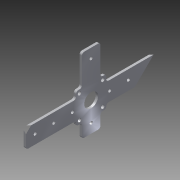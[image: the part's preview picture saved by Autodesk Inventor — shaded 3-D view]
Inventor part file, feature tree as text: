
AUTODESK INVENTOR PART (.ipt)
format: ipt  version: 2014 SP1 (Build 180222100, 222)  size: 162,816 bytes
history: native  units: in
note: dims shown in document units (in); Inventor stores cm internally (conversion verified against a paired STEP export)
features: extrude x2, sketch x2
ambient origin geometry x8: Origin, YZ Plane, XZ Plane, XY Plane, X Axis, Y Axis, Z Axis, Center Point
bodies: Solid1 (feature_tree)
feature tree (4):
  extrude  "Extrusion1"  Depth=4.0in
  extrude  "Extrusion2"  Depth=1.625in
  sketch  "Sketch1"  dims[d0=1.0in d1=4.0in]
  sketch  "Sketch2"  dims[d2=1.625in d3=1.625in d5=0.164in d6=0.164in d7=1.25in d8=1.25in d10=0.1875in d11=0.5in d12=0.5in d13=0.5in d15=0.188in d16=0.7874in d18=1.25in d19=0.7874in d21=1.25in d24=0.75in d25=0.8125in d26=0.8125in d27=0.125in d28=0.0in d29=2.44in d30=0.1875in d31=0.5in d32=1.0in d33=1.0in d34=3.0in d35=1.0in d36=3.0in d37=1.625in d38=0.1875in d39=0.8125in d40=1.625in d41=0.1875in d42=0.8125in d44=0.164in d45=0.164in d46=0.5in d47=0.5in d48=1.1811in d50=1.0in d51=0.3937in d53=1.0in d55=0.5in d56=0.5in d57=1.1811in d59=1.0in d60=0.3937in d62=1.0in d64=0.375in d65=0.375in d66=0.375in d67=0.375in d68=1.0in d69=0.0in]
